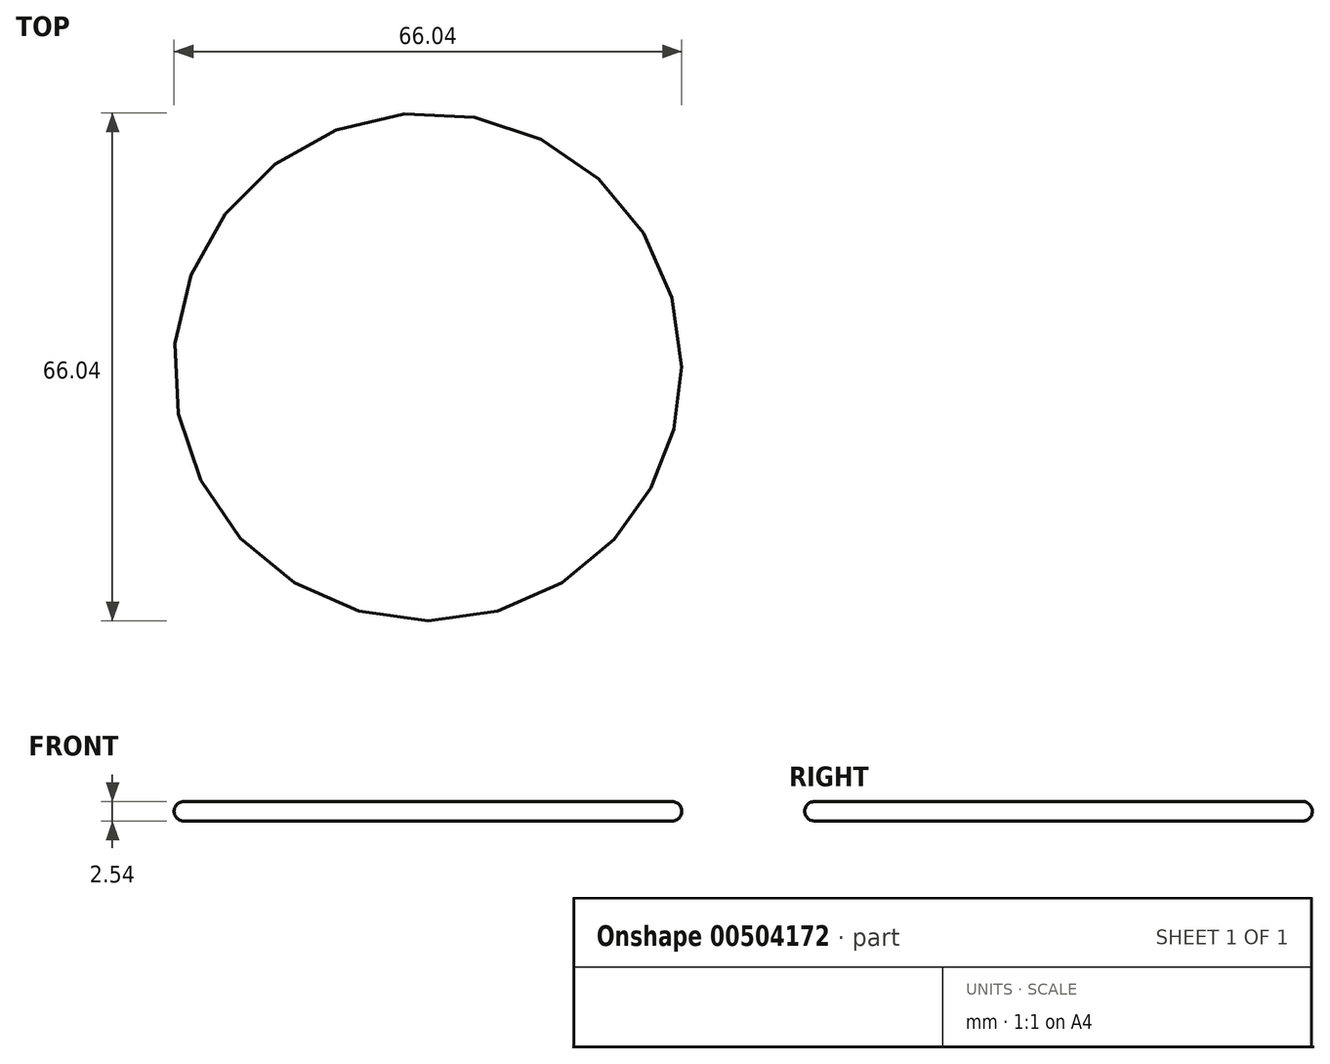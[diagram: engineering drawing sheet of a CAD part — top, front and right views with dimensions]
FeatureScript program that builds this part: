
annotation { "Feature Type Name" : "Feature", "Feature Type Description" : "" }
export const myFeature = defineFeature(function(context is Context, id is Id, definition is map)
    precondition{}
    {
        {
            var Q0;
            Q0=qCreatedBy(makeId("Top.planeOp"),FACE);
            var sketch = newSketch(context, id + "F0", { "sketchPlane" : qUnion([Q0])});
            skLineSegment(sketch, "E0", {"start": v(0, 0) * mm, "end": v(0, -33.02) * mm, "construction": true});
            skArc(sketch, "E1", {"start": v(27.46, -18.34) * mm, "mid": v(0, 33.02) * mm, "end": v(-27.46, -18.34) * mm, "construction": true});
            skLineSegment(sketch, "E2.1.0", {"start": v(0, 0) * mm, "end": v(6.44, -32.39) * mm, "construction": true});
            skLineSegment(sketch, "E2.2.0", {"start": v(0, 0) * mm, "end": v(12.64, -30.5) * mm, "construction": true});
            skLineSegment(sketch, "E2.3.0", {"start": v(0, 0) * mm, "end": v(18.34, -27.46) * mm, "construction": true});
            skLineSegment(sketch, "E2.5.0", {"start": v(0, 0) * mm, "end": v(27.46, -18.34) * mm, "construction": true});
            skLineSegment(sketch, "E2.6.0", {"start": v(0, 0) * mm, "end": v(30.5, -12.64) * mm, "construction": true});
            skLineSegment(sketch, "E2.7.0", {"start": v(0, 0) * mm, "end": v(32.39, -6.44) * mm, "construction": true});
            skLineSegment(sketch, "E2.8.0", {"start": v(0, 0) * mm, "end": v(33.02, 0) * mm, "construction": true});
            skLineSegment(sketch, "E2.9.0", {"start": v(0, 0) * mm, "end": v(32.39, 6.44) * mm, "construction": true});
            skLineSegment(sketch, "E2.10.0", {"start": v(0, 0) * mm, "end": v(30.5, 12.64) * mm, "construction": true});
            skLineSegment(sketch, "E2.11.0", {"start": v(0, 0) * mm, "end": v(27.46, 18.34) * mm, "construction": true});
            skLineSegment(sketch, "E2.12.0", {"start": v(0, 0) * mm, "end": v(23.35, 23.35) * mm, "construction": true});
            skLineSegment(sketch, "E2.13.0", {"start": v(0, 0) * mm, "end": v(18.34, 27.46) * mm, "construction": true});
            skLineSegment(sketch, "E2.14.0", {"start": v(0, 0) * mm, "end": v(12.64, 30.5) * mm, "construction": true});
            skLineSegment(sketch, "E2.15.0", {"start": v(0, 0) * mm, "end": v(6.44, 32.39) * mm, "construction": true});
            skLineSegment(sketch, "E2.16.0", {"start": v(0, 0) * mm, "end": v(0, 33.02) * mm, "construction": true});
            skLineSegment(sketch, "E2.17.0", {"start": v(0, 0) * mm, "end": v(-6.44, 32.39) * mm, "construction": true});
            skLineSegment(sketch, "E2.18.0", {"start": v(0, 0) * mm, "end": v(-12.64, 30.5) * mm, "construction": true});
            skLineSegment(sketch, "E2.19.0", {"start": v(0, 0) * mm, "end": v(-18.34, 27.46) * mm, "construction": true});
            skLineSegment(sketch, "E2.20.0", {"start": v(0, 0) * mm, "end": v(-23.35, 23.35) * mm, "construction": true});
            skLineSegment(sketch, "E2.21.0", {"start": v(0, 0) * mm, "end": v(-27.46, 18.34) * mm, "construction": true});
            skLineSegment(sketch, "E2.22.0", {"start": v(0, 0) * mm, "end": v(-30.5, 12.64) * mm, "construction": true});
            skLineSegment(sketch, "E2.23.0", {"start": v(0, 0) * mm, "end": v(-32.39, 6.44) * mm, "construction": true});
            skLineSegment(sketch, "E2.24.0", {"start": v(0, 0) * mm, "end": v(-33.02, 0) * mm, "construction": true});
            skLineSegment(sketch, "E2.25.0", {"start": v(0, 0) * mm, "end": v(-32.39, -6.44) * mm, "construction": true});
            skLineSegment(sketch, "E2.26.0", {"start": v(0, 0) * mm, "end": v(-30.5, -12.64) * mm, "construction": true});
            skLineSegment(sketch, "E2.27.0", {"start": v(0, 0) * mm, "end": v(-27.46, -18.34) * mm, "construction": true});
            skLineSegment(sketch, "E2.29.0", {"start": v(0, 0) * mm, "end": v(-18.34, -27.46) * mm, "construction": true});
            skLineSegment(sketch, "E2.30.0", {"start": v(0, 0) * mm, "end": v(-12.64, -30.5) * mm, "construction": true});
            skLineSegment(sketch, "E2.31.0", {"start": v(0, 0) * mm, "end": v(-6.44, -32.39) * mm, "construction": true});
            skPoint(sketch, "E3", {"position": v(0, 33.02) * mm});
            skPoint(sketch, "E4", {"position": v(5.57, 28.03) * mm});
            skPoint(sketch, "E5", {"position": v(12.64, 30.5) * mm});
            skPoint(sketch, "E6", {"position": v(15.88, 23.76) * mm});
            skPoint(sketch, "E7", {"position": v(23.35, 23.35) * mm});
            skPoint(sketch, "E8", {"position": v(23.76, 15.88) * mm});
            skPoint(sketch, "E9", {"position": v(-5.57, 28.03) * mm});
            skPoint(sketch, "E10", {"position": v(-15.88, 23.76) * mm});
            skPoint(sketch, "E11", {"position": v(-23.76, 15.88) * mm});
            skPoint(sketch, "E12", {"position": v(28.03, 5.57) * mm});
            skPoint(sketch, "E13", {"position": v(20.2, -20.2) * mm});
            skPoint(sketch, "E14", {"position": v(-20.2, -20.2) * mm});
            skArc(sketch, "E15.trimOffspring", {"start": v(-15.88, -23.76) * mm, "mid": v(0, -28.57) * mm, "end": v(15.88, -23.76) * mm, "construction": true});
            skArc(sketch, "E16.trimOffspring", {"start": v(28.58, 0) * mm, "mid": v(0, 28.58) * mm, "end": v(-28.58, 0) * mm, "construction": true});
            skArc(sketch, "E17.trimOffspring", {"start": v(-6.44, -32.39) * mm, "mid": v(0, -33.02) * mm, "end": v(6.44, -32.39) * mm, "construction": true});
            skCircle(sketch, "E18", {"center": v(0, 0) * mm, "radius": 15.88 * mm, "construction": true});
            skCircle(sketch, "E19", {"center": v(0, 0) * mm, "radius": 12.7 * mm, "construction": true});
            skCircle(sketch, "E20", {"center": v(0, 0) * mm, "radius": 9.53 * mm, "construction": true});
            skCircle(sketch, "E21", {"center": v(0, 0) * mm, "radius": 6.35 * mm, "construction": true});
            skLineSegment(sketch, "E22", {"start": v(14.67, 6.08) * mm, "end": v(4.74, 6.08) * mm, "construction": true});
            skLineSegment(sketch, "E23", {"start": v(-1.85, 6.08) * mm, "end": v(-9.1, 6.08) * mm});
            skLineSegment(sketch, "E24", {"start": v(-9.1, 3.77) * mm, "end": v(-9.1, 6.08) * mm});
            skLineSegment(sketch, "E25", {"start": v(-9.1, 3.77) * mm, "end": v(-5.28, 3.53) * mm});
            skLineSegment(sketch, "E26", {"start": v(-5.28, 3.53) * mm, "end": v(0, 0) * mm});
            skLineSegment(sketch, "E27", {"start": v(0, 0) * mm, "end": v(5.28, 3.53) * mm});
            skLineSegment(sketch, "E28", {"start": v(5.28, 3.53) * mm, "end": v(7.92, 5.3) * mm});
            skLineSegment(sketch, "E29", {"start": v(7.92, 6.08) * mm, "end": v(4.74, 6.08) * mm});
            skLineSegment(sketch, "E30", {"start": v(7.92, 6.08) * mm, "end": v(7.92, 9.93) * mm});
            skLineSegment(sketch, "E31", {"start": v(7.92, 9.93) * mm, "end": v(4.74, 9.93) * mm});
            skLineSegment(sketch, "E32", {"start": v(4.74, 9.93) * mm, "end": v(4.74, 6.08) * mm});
            skLineSegment(sketch, "E33", {"start": v(4.06, 6.08) * mm, "end": v(4.06, 11.16) * mm});
            skLineSegment(sketch, "E34", {"start": v(4.06, 11.16) * mm, "end": v(0.88, 11.16) * mm});
            skLineSegment(sketch, "E35", {"start": v(0.88, 11.16) * mm, "end": v(0.88, 6.08) * mm});
            skLineSegment(sketch, "E36", {"start": v(0.2, 6.08) * mm, "end": v(0.2, 11.8) * mm});
            skLineSegment(sketch, "E37", {"start": v(0.2, 11.8) * mm, "end": v(-2.98, 11.8) * mm});
            skLineSegment(sketch, "E38", {"start": v(-2.98, 11.8) * mm, "end": v(-2.98, 9.94) * mm});
            skLineSegment(sketch, "E39", {"start": v(-2.98, 6.08) * mm, "end": v(-3.66, 6.08) * mm});
            skLineSegment(sketch, "E40", {"start": v(-1.85, 6.08) * mm, "end": v(-1.85, 9.25) * mm});
            skLineSegment(sketch, "E41", {"start": v(-1.85, 9.25) * mm, "end": v(-10.74, 9.25) * mm});
            skLineSegment(sketch, "E42", {"start": v(-10.74, 9.25) * mm, "end": v(-10.74, 2.14) * mm});
            skLineSegment(sketch, "E43", {"start": v(-1.2, 6.08) * mm, "end": v(-1.16, 6.08) * mm});
            skLineSegment(sketch, "E44", {"start": v(-1.16, 6.08) * mm, "end": v(-1.16, 9.94) * mm});
            skLineSegment(sketch, "E45", {"start": v(-1.16, 9.94) * mm, "end": v(-2.98, 9.94) * mm});
            skLineSegment(sketch, "E46", {"start": v(-3.66, 9.94) * mm, "end": v(-3.66, 11.2) * mm});
            skLineSegment(sketch, "E47", {"start": v(-3.66, 11.2) * mm, "end": v(-6.84, 11.2) * mm});
            skLineSegment(sketch, "E48", {"start": v(-6.84, 11.2) * mm, "end": v(-6.84, 9.94) * mm});
            skLineSegment(sketch, "E49.trimOffspring", {"start": v(4.06, 6.08) * mm, "end": v(0.88, 6.08) * mm, "construction": true});
            skLineSegment(sketch, "E50.trimOffspring", {"start": v(4.06, 6.08) * mm, "end": v(0.88, 6.08) * mm});
            skLineSegment(sketch, "E51.trimOffspring", {"start": v(0.2, 6.08) * mm, "end": v(-1.2, 6.08) * mm, "construction": true});
            skLineSegment(sketch, "E52.trimOffspring", {"start": v(0.2, 6.08) * mm, "end": v(-1.2, 6.08) * mm});
            skLineSegment(sketch, "E53.trimOffspring", {"start": v(-1.85, 6.08) * mm, "end": v(-14.67, 6.08) * mm, "construction": true});
            skLineSegment(sketch, "E54.trimOffspring", {"start": v(-3.66, 9.94) * mm, "end": v(-6.84, 9.94) * mm});
            skLineSegment(sketch, "E55", {"start": v(7.92, 5.3) * mm, "end": v(7.92, 1.58) * mm});
            skLineSegment(sketch, "E56", {"start": v(7.92, 1.58) * mm, "end": v(7.92, 0) * mm});
            skLineSegment(sketch, "E57", {"start": v(-10.74, 2.14) * mm, "end": v(-10.74, 0) * mm});
            skLineSegment(sketch, "E58", {"start": v(7.92, 0) * mm, "end": v(7.92, -1.58) * mm});
            skLineSegment(sketch, "E59", {"start": v(7.92, -1.58) * mm, "end": v(3.55, -5.32) * mm});
            skLineSegment(sketch, "E60", {"start": v(3.55, -5.32) * mm, "end": v(10.48, -24.52) * mm});
            skLineSegment(sketch, "E61", {"start": v(-10.74, 0) * mm, "end": v(-10.74, -2.14) * mm});
            skLineSegment(sketch, "E62", {"start": v(-10.74, -2.14) * mm, "end": v(-3.58, -5.35) * mm});
            skLineSegment(sketch, "E63", {"start": v(-3.58, -5.35) * mm, "end": v(-10.48, -24.52) * mm});
            skCircle(sketch, "E64", {"center": v(0, 0) * mm, "radius": 22.23 * mm, "construction": true});
            skLineSegment(sketch, "E65", {"start": v(0, 28.58) * mm, "end": v(4.34, 21.8) * mm});
            skLineSegment(sketch, "E66", {"start": v(4.34, 21.8) * mm, "end": v(10.94, 26.4) * mm});
            skLineSegment(sketch, "E67", {"start": v(10.94, 26.4) * mm, "end": v(12.35, 18.48) * mm});
            skLineSegment(sketch, "E68", {"start": v(12.35, 18.48) * mm, "end": v(20.2, 20.2) * mm});
            skLineSegment(sketch, "E69", {"start": v(20.2, 20.2) * mm, "end": v(18.48, 12.35) * mm});
            skLineSegment(sketch, "E70", {"start": v(18.48, 12.35) * mm, "end": v(26.4, 10.94) * mm});
            skLineSegment(sketch, "E71", {"start": v(26.4, 10.94) * mm, "end": v(21.84, 4.11) * mm});
            skLineSegment(sketch, "E72", {"start": v(21.84, 4.11) * mm, "end": v(28.58, 0) * mm});
            skLineSegment(sketch, "E73", {"start": v(28.57, 0) * mm, "end": v(21.8, -4.34) * mm});
            skLineSegment(sketch, "E74.MirrorCS", {"start": v(0, 28.58) * mm, "end": v(-4.34, 21.8) * mm});
            skLineSegment(sketch, "E75.MirrorCS", {"start": v(-4.34, 21.8) * mm, "end": v(-10.94, 26.4) * mm});
            skLineSegment(sketch, "E76.MirrorCS", {"start": v(-10.94, 26.4) * mm, "end": v(-12.35, 18.48) * mm});
            skLineSegment(sketch, "E77.MirrorCS", {"start": v(-12.35, 18.48) * mm, "end": v(-20.2, 20.2) * mm});
            skLineSegment(sketch, "E78.MirrorCS", {"start": v(-20.2, 20.2) * mm, "end": v(-18.48, 12.35) * mm});
            skLineSegment(sketch, "E79.MirrorCS", {"start": v(-18.48, 12.35) * mm, "end": v(-26.4, 10.94) * mm});
            skLineSegment(sketch, "E80.MirrorCS", {"start": v(-26.4, 10.94) * mm, "end": v(-21.84, 4.11) * mm});
            skLineSegment(sketch, "E81.MirrorCS", {"start": v(-21.84, 4.11) * mm, "end": v(-28.57, 0) * mm});
            skLineSegment(sketch, "E82.MirrorCS", {"start": v(-28.58, 0) * mm, "end": v(-21.8, -4.34) * mm});
            skArc(sketch, "E83.0", {"start": v(-21.8, -4.34) * mm, "mid": v(-19.6, -10.48) * mm, "end": v(-15.72, -15.72) * mm});
            skArc(sketch, "E84.0", {"start": v(15.72, -15.72) * mm, "mid": v(19.6, -10.48) * mm, "end": v(21.8, -4.34) * mm});
            skArc(sketch, "E85.0", {"start": v(10.48, -24.52) * mm, "mid": v(14.94, -22.1) * mm, "end": v(18.86, -18.86) * mm});
            skArc(sketch, "E86.0", {"start": v(-18.86, -18.86) * mm, "mid": v(-14.94, -22.1) * mm, "end": v(-10.48, -24.52) * mm});
            skLineSegment(sketch, "E87", {"start": v(18.86, -18.86) * mm, "end": v(15.72, -15.72) * mm});
            skLineSegment(sketch, "E88", {"start": v(-18.86, -18.86) * mm, "end": v(-15.72, -15.72) * mm});
            skCircle(sketch, "E89", {"center": v(0, 0) * mm, "radius": 33.02 * mm});
            skSolve(sketch);
        }
        {
            var Q0;
            {var subQ0=sQuery(id+"F0.wireOp",EDGE,"E24");Q0=makeQuery(id+"F0.imprint","IMPRINT",FACE,{"disambiguationData":[TD([[makeQuery(id+"F0.imprint","IMPRINT",EDGE,{"derivedFrom":subQ0}),1.0]])]});}
            var Q1;
            Q1=makeQuery(id+"F0.imprint","IMPRINT",FACE,{"disambiguationData":[TD([[makeQuery(id+"F0.imprint","IMPRINT",EDGE,{"derivedFrom":sQuery(id+"F0.wireOp",EDGE,"E29")}),-1.0]])]});
            var Q2;
            Q2=makeQuery(id+"F0.imprint","IMPRINT",FACE,{"disambiguationData":[TD([[makeQuery(id+"F0.imprint","IMPRINT",EDGE,{"derivedFrom":sQuery(id+"F0.wireOp",EDGE,"E33")}),1.0]])]});
            var Q3;
            {var subQ2=sQuery(id+"F0.wireOp",EDGE,"E36");Q3=makeQuery(id+"F0.imprint","IMPRINT",FACE,{"disambiguationData":[TD([[makeQuery(id+"F0.imprint","IMPRINT",EDGE,{"derivedFrom":subQ2}),1.0]])]});}
            var Q4;
            Q4=makeQuery(id+"F0.imprint","IMPRINT",FACE,{"disambiguationData":[TD([[makeQuery(id+"F0.imprint","IMPRINT",EDGE,{"derivedFrom":sQuery(id+"F0.wireOp",EDGE,"E46")}),1.0]])]});
            extrude(context, id + "F1", {"entities" : qUnion([Q0, Q1, Q2, Q3, Q4]), "depth" : 1.27 * mm});
        }
        {
            var Q0;
            {var subQ6=sQuery(id+"F0.wireOp",EDGE,"E24");Q0=makeQuery(id+"F0.imprint","IMPRINT",FACE,{"disambiguationData":[TD([[makeQuery(id+"F0.imprint","IMPRINT",EDGE,{"derivedFrom":subQ6}),-1.0]])]});}
            extrude(context, id + "F2", {"entities" : qUnion([Q0]), "depth" : 1.27 * mm});
        }
        {
            var Q0;
            {var subQ0=sQuery(id+"F0.wireOp",EDGE,"E24");Q0=makeQuery(id+"F0.imprint","IMPRINT",FACE,{"disambiguationData":[TD([[makeQuery(id+"F0.imprint","IMPRINT",EDGE,{"derivedFrom":subQ0}),1.0]])]});}
            var Q1;
            {var subQ6=sQuery(id+"F0.wireOp",EDGE,"E24");Q1=makeQuery(id+"F0.imprint","IMPRINT",FACE,{"disambiguationData":[TD([[makeQuery(id+"F0.imprint","IMPRINT",EDGE,{"derivedFrom":subQ6}),-1.0]])]});}
            var Q2;
            Q2=makeQuery(id+"F0.imprint","IMPRINT",FACE,{"disambiguationData":[TD([[makeQuery(id+"F0.imprint","IMPRINT",EDGE,{"derivedFrom":sQuery(id+"F0.wireOp",EDGE,"E29")}),-1.0]])]});
            var Q3;
            Q3=makeQuery(id+"F0.imprint","IMPRINT",FACE,{"disambiguationData":[TD([[makeQuery(id+"F0.imprint","IMPRINT",EDGE,{"derivedFrom":sQuery(id+"F0.wireOp",EDGE,"E33")}),1.0]])]});
            var Q4;
            {var subQ2=sQuery(id+"F0.wireOp",EDGE,"E36");Q4=makeQuery(id+"F0.imprint","IMPRINT",FACE,{"disambiguationData":[TD([[makeQuery(id+"F0.imprint","IMPRINT",EDGE,{"derivedFrom":subQ2}),1.0]])]});}
            var Q5;
            Q5=makeQuery(id+"F0.imprint","IMPRINT",FACE,{"disambiguationData":[TD([[makeQuery(id+"F0.imprint","IMPRINT",EDGE,{"derivedFrom":sQuery(id+"F0.wireOp",EDGE,"E46")}),1.0]])]});
            extrude(context, id + "F3", {"entities" : qUnion([Q0, Q1, Q2, Q3, Q4, Q5]), "operationType" : NewBodyOperationType.ADD, "oppositeDirection" : true, "depth" : 1.27 * mm});
        }
        {
            var Q0;
            Q0=makeQuery(id+"F1.opExtrude","SWEPT_FACE",FACE,{"disambiguationData":[OSD([sQuery(id+"F0.wireOp",EDGE,"E89")])]});
            fillet(context, id + "F4", {"entities" : qUnion([Q0]), "radius" : 1.27 * mm, "tangentPropagation" : true, "allowEdgeOverflow" : false});
        }
    });
